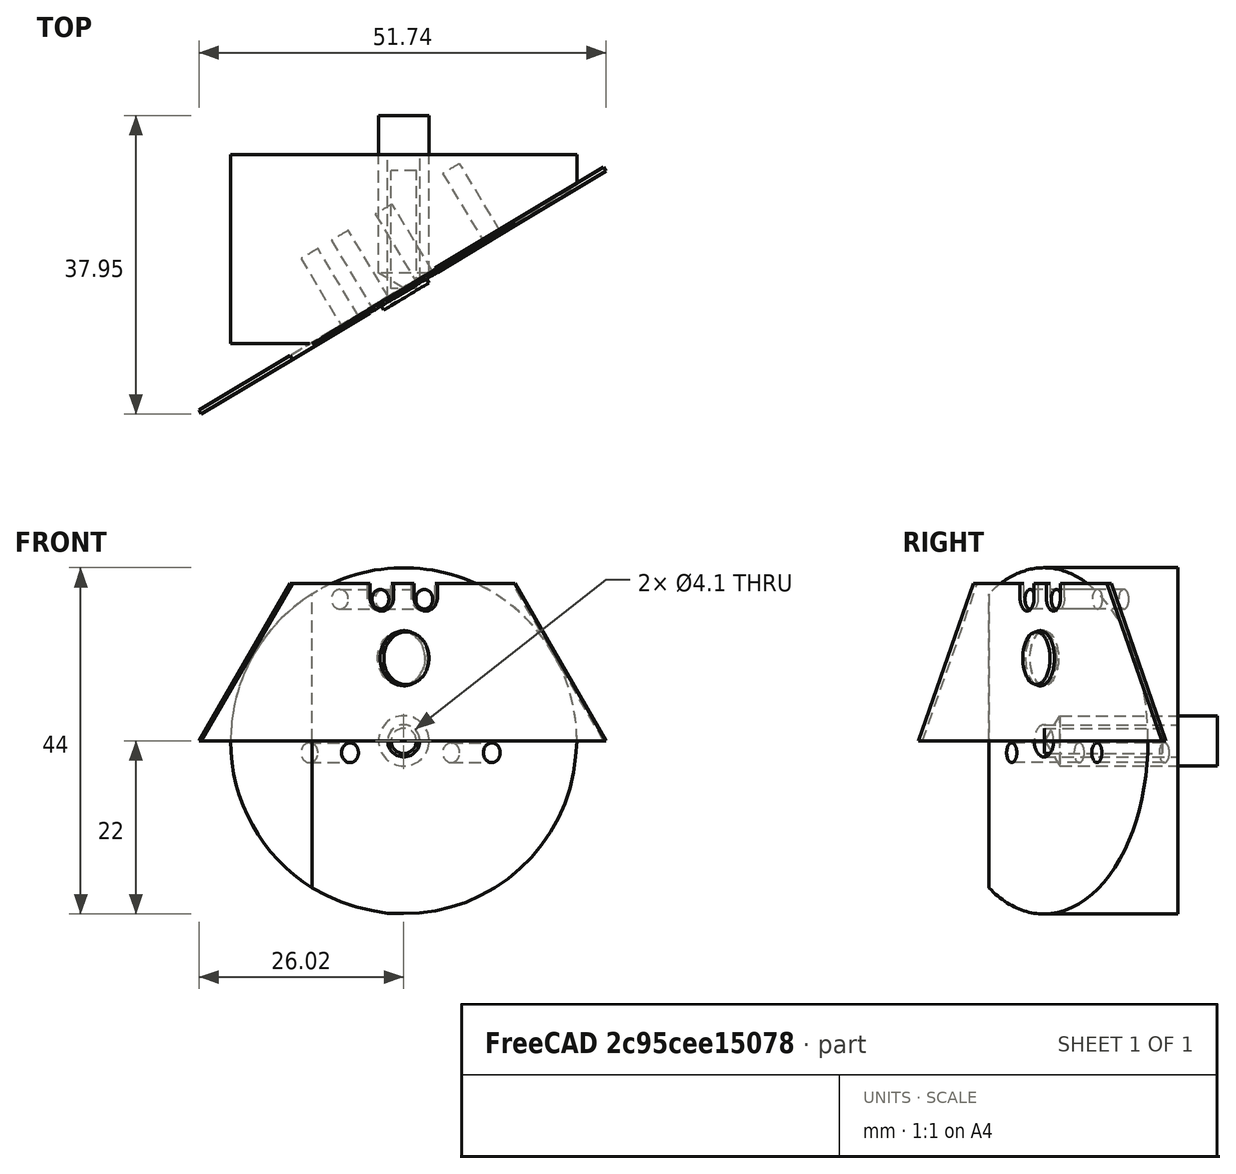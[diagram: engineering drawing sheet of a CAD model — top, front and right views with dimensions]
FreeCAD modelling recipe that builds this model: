
FCSTD DOCUMENT  (FreeCAD 0.16R5480 (Git))
Label: PTFEAngleCutJig-4mm
License: All rights reserved
LicenseURL: http://en.wikipedia.org/wiki/All_rights_reserved
objects: Sketcher::SketchObject×5, PartDesign::Revolution×2, PartDesign::Pad×2, Mesh::Feature×2, Part::Cylinder×1, Part::Cut×1, Part::Feature×1, Part::Sphere×1, Part::MultiCommon×1, PartDesign::Pocket×1
note: 20 computed .brp shape members not serialized (recipe doc carries the construction recipe); baked Part::Feature solids carry a one-line shape summary decoded from their .brp

FEATURE [Sketcher::SketchObject] Sketch
  sketch-geometry (4):
    g0: LineSegment StartX=0 StartY=-1.92275 StartZ=0 EndX=3.2 EndY=0 EndZ=0
    g1: LineSegment StartX=3.2 StartY=0 StartZ=0 EndX=3.2 EndY=20 EndZ=0
    g2: LineSegment StartX=3.2 StartY=20 StartZ=0 EndX=0 EndY=20 EndZ=0
    g3: LineSegment StartX=0 StartY=20 StartZ=0 EndX=0 EndY=-1.92275 EndZ=0
  constraints (13):
    c: PointOnObject(g0,g-2)
    c: PointOnObject(g0,g-1)
    c: Coincident(g0,g1)
    c: Vertical(g1)
    c: DistanceY(g1,g1) = 20
    c: DistanceX(g1) = 3.2
    c: Angle(g1,g0) = 2.11185
    c: Coincident(g2,g1)
    c: PointOnObject(g2,g-2)
    c: Horizontal(g2)
    c: Coincident(g3,g0)
    c: Vertical(g3)
    c: Coincident(g2,g3)
FEATURE [PartDesign::Revolution] Revolution  label="Drill"
  Angle = 360
  Axis = (0,1,0)
  Base = (0,0,0)
  ReferenceAxis = -> Sketch [V_Axis]
  Reversed = true
  Sketch = -> Sketch
FEATURE [Part::Cylinder] Cylinder
  Angle = 360
  Height = 15
  Placement = pos=(0,-2,0) rot=(-1,0,0;1.5708rad)
  Radius = 1.6
FEATURE [Sketcher::SketchObject] Sketch001
  sketch-geometry (6):
    g0: LineSegment StartX=0 StartY=-9 StartZ=0 EndX=0 EndY=-5 EndZ=0
    g1: LineSegment StartX=0 StartY=-5 StartZ=0 EndX=2.05 EndY=-5 EndZ=0
    g2: LineSegment StartX=2.05 StartY=-5 StartZ=0 EndX=2.05 EndY=15 EndZ=0
    g3: LineSegment StartX=2.05 StartY=15 StartZ=0 EndX=22 EndY=15 EndZ=0
    g4: LineSegment StartX=22 StartY=15 StartZ=0 EndX=22 EndY=-9 EndZ=0
    g5: LineSegment StartX=22 StartY=-9 StartZ=0 EndX=0 EndY=-9 EndZ=0
  constraints (18):
    c: PointOnObject(g0,g-2)
    c: Vertical(g0)
    c: Coincident(g0,g1)
    c: Horizontal(g1)
    c: Coincident(g1,g2)
    c: Vertical(g2)
    c: Coincident(g2,g3)
    c: Horizontal(g3)
    c: Coincident(g3,g4)
    c: Vertical(g4)
    c: Coincident(g4,g5)
    c: Coincident(g5,g0)
    c: Horizontal(g5)
    c: DistanceY(g1) = -5
    c: DistanceY(g4) = -9
    c: DistanceX(g1) = 2.05
    c: DistanceX(g4) = 22
    c: DistanceY(g2,g2) = 20
FEATURE [Sketcher::SketchObject] Sketch002
  sketch-geometry (3):
    g0: LineSegment StartX=25 StartY=13 StartZ=0 EndX=-11.6141 EndY=-9 EndZ=0
    g1: LineSegment StartX=25 StartY=13 StartZ=0 EndX=25 EndY=-9 EndZ=0
    g2: LineSegment StartX=25 StartY=-9 StartZ=0 EndX=-11.6141 EndY=-9 EndZ=0
  constraints (9):
    c: Coincident(g1,g0)
    c: Vertical(g1)
    c: Coincident(g2,g1)
    c: Coincident(g2,g0)
    c: Horizontal(g2)
    c: DistanceX(g1) = 25
    c: DistanceY(g1) = -9
    c: Angle(g0,g1) = 1.02974
    c: DistanceY(g0) = 13
FEATURE [PartDesign::Pad] Pad
  Length = 50
  Length2 = 100
  Midplane = true
  Sketch = -> Sketch002
  Type = 0
FEATURE [PartDesign::Revolution] Revolution001
  Angle = 360
  Axis = (0,1,0)
  Base = (0,0,0)
  ReferenceAxis = -> Sketch001 [V_Axis]
  Reversed = true
  Sketch = -> Sketch001
FEATURE [Part::Cut] Cut
  Base = -> Revolution001
  Tool = -> Pad
FEATURE [Part::Feature] Pocket001  label="Blade-Cutouts001"
  Placement = pos=(0,0,0) rot=(-1,0,0;1.5708rad)
  shape: bbox 60 x 0.6 x 20 mm, 15 faces (baked)
FEATURE [Part::Sphere] Sphere
  Angle1 = -90
  Angle2 = 90
  Angle3 = 360
  Radius = 50
FEATURE [Part::MultiCommon] Common
  Placement = pos=(0,-2.5,20) rot=(0,0,1;0.541052rad)
  Shapes = -> [Pocket001,Sphere]
FEATURE [Sketcher::SketchObject] Sketch003
  Placement = pos=(0.892446,-1.48528,0) rot=(0.930961,0.258178,0.258178;1.64227rad)
  Support = -> Cut [Face2]
  sketch-geometry (4):
    g0: Circle CenterX=-4.5 CenterY=18 CenterZ=0 NormalX=0 NormalY=0 NormalZ=1 Radius=1.25
    g1: Circle CenterX=2 CenterY=18 CenterZ=0 NormalX=0 NormalY=0 NormalZ=1 Radius=1.25
    g2: Circle CenterX=12 CenterY=-1.5 CenterZ=0 NormalX=0 NormalY=0 NormalZ=1 Radius=1.25
    g3: Circle CenterX=-9 CenterY=-1.5 CenterZ=0 NormalX=0 NormalY=0 NormalZ=1 Radius=1.25
  constraints (12):
    c: DistanceX(g0,g1) = 6.5
    c: DistanceY(g1) = 18
    c: DistanceY(g1,g0) = 0
    c: Radius(g1) = 1.25
    c: DistanceX(g1) = 2
    c: Radius(g2) = 1.25
    c: Equal(g2,g3)
    c: DistanceX(g2) = 12
    c: DistanceX(g3) = -9
    c: DistanceY(g3,g2) = 0
    c: DistanceY(g2) = -1.5
    c: Equal(g0,g1)
FEATURE [PartDesign::Pocket] Pocket
  Length = 10
  Sketch = -> Sketch003
  Type = 0
FEATURE [Sketcher::SketchObject] Sketch004
  Placement = pos=(0.892446,-1.48528,0) rot=(0.930961,0.258178,0.258178;1.64227rad)
  Support = -> Pocket [Face2]
  sketch-geometry (1):
    g0: Circle CenterX=-1.25 CenterY=10.5 CenterZ=0 NormalX=0 NormalY=0 NormalZ=1 Radius=3.35
  constraints (3):
    c: DistanceX(g0) = -1.25
    c: DistanceY(g0) = 10.5
    c: Radius(g0) = 3.35
FEATURE [PartDesign::Pad] Pad001
  Length = 1
  Length2 = 100
  Sketch = -> Sketch004
  Type = 0
FEATURE [Mesh::Feature] Mesh  label="Pad001 (Meshed)"
FEATURE [Mesh::Feature] Mesh001  label="Pocket (Meshed)"
